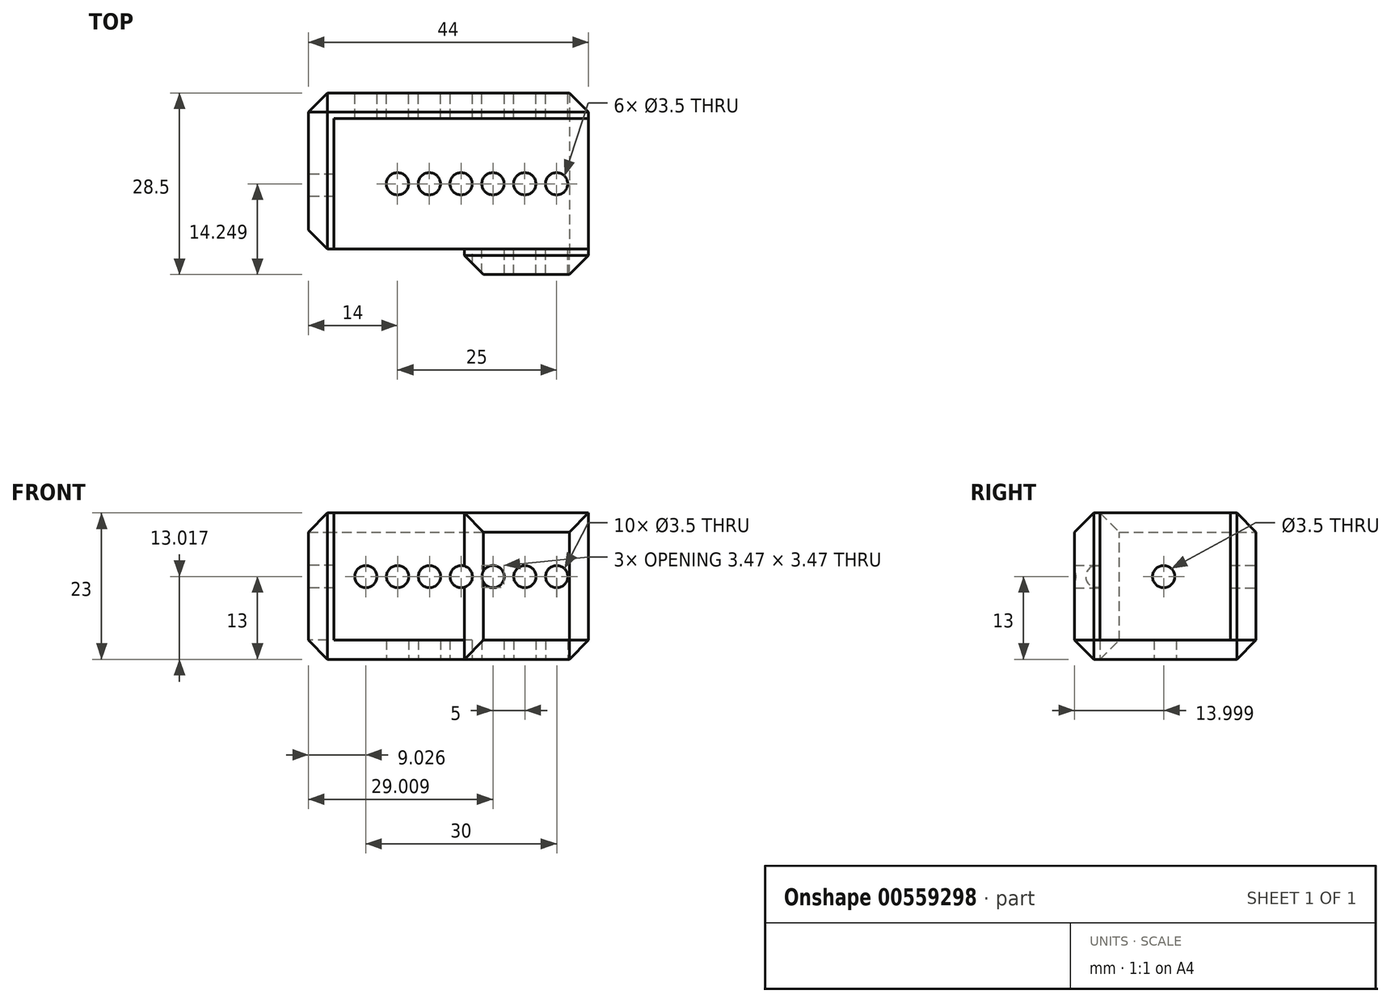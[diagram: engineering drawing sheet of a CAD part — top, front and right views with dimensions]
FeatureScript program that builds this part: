
annotation { "Feature Type Name" : "Feature", "Feature Type Description" : "" }
export const myFeature = defineFeature(function(context is Context, id is Id, definition is map)
    precondition{}
    {
        {
            var Q0;
            Q0=qCreatedBy(makeId("Top.planeOp"),FACE);
            var sketch = newSketch(context, id + "F0", { "sketchPlane" : qUnion([Q0])});
            skLineSegment(sketch, "E0", {"start": v(-54.8, 23.52) * mm, "end": v(-54.8, 3.02) * mm});
            skLineSegment(sketch, "E1", {"start": v(-54.8, 23.52) * mm, "end": v(-14.8, 23.52) * mm});
            skLineSegment(sketch, "E2", {"start": v(-54.8, 3.02) * mm, "end": v(-14.8, 3.02) * mm});
            skLineSegment(sketch, "E3", {"start": v(-14.8, 3.02) * mm, "end": v(-14.8, 23.52) * mm});
            skLineSegment(sketch, "E4", {"start": v(-58.8, 3.02) * mm, "end": v(-54.8, 3.02) * mm});
            skLineSegment(sketch, "E5", {"start": v(-14.8, 23.52) * mm, "end": v(-14.8, 27.52) * mm});
            skLineSegment(sketch, "E6", {"start": v(-14.8, 27.52) * mm, "end": v(-58.8, 27.52) * mm});
            skLineSegment(sketch, "E7", {"start": v(-58.8, 27.52) * mm, "end": v(-58.8, 3.02) * mm});
            skLineSegment(sketch, "E8", {"start": v(-54.8, 23.52) * mm, "end": v(-34.8, 3.02) * mm, "construction": true});
            skLineSegment(sketch, "E9", {"start": v(-34.8, 3.02) * mm, "end": v(-14.8, 23.52) * mm, "construction": true});
            skLineSegment(sketch, "E10", {"start": v(-14.8, 3.02) * mm, "end": v(-34.8, 23.52) * mm, "construction": true});
            skLineSegment(sketch, "E11", {"start": v(-34.8, 23.52) * mm, "end": v(-54.8, 3.02) * mm, "construction": true});
            skCircle(sketch, "E12", {"center": v(-24.8, 13.27) * mm, "radius": 1.75 * mm});
            skLineSegment(sketch, "E13", {"start": v(-24.8, 13.27) * mm, "end": v(-29.8, 13.27) * mm});
            skLineSegment(sketch, "E14", {"start": v(-29.8, 13.27) * mm, "end": v(-34.8, 13.27) * mm});
            skLineSegment(sketch, "E15", {"start": v(-34.8, 13.27) * mm, "end": v(-39.8, 13.27) * mm});
            skLineSegment(sketch, "E16", {"start": v(-39.8, 13.27) * mm, "end": v(-44.8, 13.27) * mm});
            skLineSegment(sketch, "E17", {"start": v(-24.8, 13.27) * mm, "end": v(-19.8, 13.27) * mm});
            skLineSegment(sketch, "E18", {"start": v(-19.8, 13.27) * mm, "end": v(-14.8, 13.27) * mm});
            skCircle(sketch, "E19", {"center": v(-39.8, 13.27) * mm, "radius": 1.75 * mm});
            skCircle(sketch, "E20", {"center": v(-34.8, 13.27) * mm, "radius": 1.75 * mm});
            skCircle(sketch, "E21", {"center": v(-19.8, 13.27) * mm, "radius": 1.75 * mm});
            skCircle(sketch, "E22", {"center": v(-29.8, 13.27) * mm, "radius": 1.75 * mm});
            skCircle(sketch, "E23", {"center": v(-44.8, 13.27) * mm, "radius": 1.75 * mm});
            skLineSegment(sketch, "E24", {"start": v(-14.8, 3.02) * mm, "end": v(-14.8, -0.98) * mm});
            skLineSegment(sketch, "E25", {"start": v(-14.8, -0.98) * mm, "end": v(-34.3, -0.98) * mm});
            skLineSegment(sketch, "E26", {"start": v(-34.3, -0.98) * mm, "end": v(-34.3, 3.02) * mm});
            skSolve(sketch);
        }
        {
            var Q0;
            Q0=makeQuery(id+"F0.imprint","IMPRINT",FACE,{"disambiguationData":[TD([[makeQuery(id+"F0.imprint","IMPRINT",EDGE,{"derivedFrom":sQuery(id+"F0.wireOp",EDGE,"E0")}),1.0]])]});
            extrude(context, id + "F1", {"entities" : qUnion([Q0]), "depth" : 3 * mm, "offsetDistance" : 25 * mm});
        }
        {
            var Q0;
            Q0=makeQuery(id+"F0.imprint","IMPRINT",FACE,{"disambiguationData":[TD([[makeQuery(id+"F0.imprint","IMPRINT",EDGE,{"derivedFrom":sQuery(id+"F0.wireOp",EDGE,"E0")}),-1.0]])]});
            var Q1;
            {var subQ0=sQuery(id+"F0.wireOp",EDGE,"E24");Q1=makeQuery(id+"F0.imprint","IMPRINT",FACE,{"disambiguationData":[TD([[makeQuery(id+"F0.imprint","IMPRINT",EDGE,{"derivedFrom":subQ0}),-1.0]])]});}
            extrude(context, id + "F2", {"entities" : qUnion([Q0, Q1]), "operationType" : NewBodyOperationType.ADD, "depth" : 23 * mm, "offsetDistance" : 25 * mm});
        }
        {
            var Q0;
            Q0=makeQuery(id+"F2.opExtrude","SWEPT_FACE",FACE,{"disambiguationData":[OSD([sQuery(id+"F0.wireOp",EDGE,"E6")])]});
            var sketch = newSketch(context, id + "F3", { "sketchPlane" : qUnion([Q0])});
            skLineSegment(sketch, "E27.bottom", {"start": v(14.8, 23) * mm, "end": v(58.8, 23) * mm});
            skLineSegment(sketch, "E27.top", {"start": v(14.8, 3) * mm, "end": v(58.8, 3) * mm});
            skLineSegment(sketch, "E27.left", {"start": v(14.8, 23) * mm, "end": v(14.8, 3) * mm});
            skLineSegment(sketch, "E27.right", {"start": v(58.8, 23) * mm, "end": v(58.8, 3) * mm});
            skLineSegment(sketch, "E28", {"start": v(49.78, 13) * mm, "end": v(44.78, 13) * mm, "construction": true});
            skLineSegment(sketch, "E29", {"start": v(44.78, 13) * mm, "end": v(39.78, 13) * mm, "construction": true});
            skLineSegment(sketch, "E30", {"start": v(39.78, 13) * mm, "end": v(34.78, 13) * mm, "construction": true});
            skLineSegment(sketch, "E31", {"start": v(34.78, 13) * mm, "end": v(29.78, 13) * mm, "construction": true});
            skLineSegment(sketch, "E32", {"start": v(29.78, 13) * mm, "end": v(24.78, 13) * mm, "construction": true});
            skLineSegment(sketch, "E33", {"start": v(24.78, 13) * mm, "end": v(19.78, 13) * mm, "construction": true});
            skLineSegment(sketch, "E34", {"start": v(19.78, 13) * mm, "end": v(14.78, 13) * mm, "construction": true});
            skCircle(sketch, "E35", {"center": v(19.78, 13) * mm, "radius": 1.75 * mm});
            skCircle(sketch, "E36", {"center": v(24.78, 13) * mm, "radius": 1.75 * mm});
            skCircle(sketch, "E37", {"center": v(29.78, 13) * mm, "radius": 1.75 * mm});
            skCircle(sketch, "E38", {"center": v(34.78, 13) * mm, "radius": 1.75 * mm});
            skCircle(sketch, "E39", {"center": v(39.78, 13) * mm, "radius": 1.75 * mm});
            skCircle(sketch, "E40", {"center": v(44.78, 13) * mm, "radius": 1.75 * mm});
            skCircle(sketch, "E41", {"center": v(49.78, 13) * mm, "radius": 1.75 * mm});
            skLineSegment(sketch, "E42", {"start": v(49.78, 13) * mm, "end": v(58.8, 13) * mm});
            skSolve(sketch);
        }
        {
            var Q0;
            Q0=makeQuery(id+"F3.imprint","IMPRINT",FACE,{"disambiguationData":[TD([[makeQuery(id+"F3.imprint","IMPRINT",EDGE,{"derivedFrom":sQuery(id+"F3.wireOp",EDGE,"E35")}),1.0]])]});
            var Q1;
            Q1=makeQuery(id+"F3.imprint","IMPRINT",FACE,{"disambiguationData":[TD([[makeQuery(id+"F3.imprint","IMPRINT",EDGE,{"derivedFrom":sQuery(id+"F3.wireOp",EDGE,"E36")}),1.0]])]});
            var Q2;
            Q2=makeQuery(id+"F3.imprint","IMPRINT",FACE,{"disambiguationData":[TD([[makeQuery(id+"F3.imprint","IMPRINT",EDGE,{"derivedFrom":sQuery(id+"F3.wireOp",EDGE,"E37")}),1.0]])]});
            var Q3;
            Q3=makeQuery(id+"F3.imprint","IMPRINT",FACE,{"disambiguationData":[TD([[makeQuery(id+"F3.imprint","IMPRINT",EDGE,{"derivedFrom":sQuery(id+"F3.wireOp",EDGE,"E38")}),1.0]])]});
            var Q4;
            Q4=makeQuery(id+"F3.imprint","IMPRINT",FACE,{"disambiguationData":[TD([[makeQuery(id+"F3.imprint","IMPRINT",EDGE,{"derivedFrom":sQuery(id+"F3.wireOp",EDGE,"E39")}),1.0]])]});
            var Q5;
            Q5=makeQuery(id+"F3.imprint","IMPRINT",FACE,{"disambiguationData":[TD([[makeQuery(id+"F3.imprint","IMPRINT",EDGE,{"derivedFrom":sQuery(id+"F3.wireOp",EDGE,"E40")}),1.0]])]});
            var Q6;
            Q6=makeQuery(id+"F3.imprint","IMPRINT",FACE,{"disambiguationData":[TD([[makeQuery(id+"F3.imprint","IMPRINT",EDGE,{"derivedFrom":sQuery(id+"F3.wireOp",EDGE,"E41")}),1.0]])]});
            extrude(context, id + "F4", {"entities" : qUnion([Q0, Q1, Q2, Q3, Q4, Q5, Q6]), "operationType" : NewBodyOperationType.REMOVE, "endBound" : BoundingType.THROUGH_ALL, "oppositeDirection" : true, "depth" : 25 * mm, "offsetDistance" : 25 * mm});
        }
        {
            var Q0;
            Q0=makeQuery(id+"F2.opExtrude","SWEPT_FACE",FACE,{"disambiguationData":[OSD([sQuery(id+"F0.wireOp",EDGE,"E7")])]});
            var sketch = newSketch(context, id + "F5", { "sketchPlane" : qUnion([Q0])});
            skLineSegment(sketch, "E43.bottom", {"start": v(-3.02, 23) * mm, "end": v(-23.02, 23) * mm});
            skLineSegment(sketch, "E43.top", {"start": v(-3.02, 3) * mm, "end": v(-23.02, 3) * mm});
            skLineSegment(sketch, "E43.left", {"start": v(-3.02, 23) * mm, "end": v(-3.02, 3) * mm});
            skLineSegment(sketch, "E43.right", {"start": v(-23.02, 23) * mm, "end": v(-23.02, 3) * mm});
            skLineSegment(sketch, "E44", {"start": v(-23.02, 3) * mm, "end": v(-3.02, 23) * mm});
            skLineSegment(sketch, "E45", {"start": v(-3.02, 3) * mm, "end": v(-23.02, 23) * mm});
            skCircle(sketch, "E46", {"center": v(-13.02, 13) * mm, "radius": 1.75 * mm});
            skSolve(sketch);
        }
        {
            var Q0;
            {var subQ0=sQuery(id+"F5.wireOp",EDGE,"E45");var subQ1=sQuery(id+"F5.wireOp",EDGE,"E44");var subQ2=makeQuery(id+"F5.imprint","INTERSECT",VERTEX,{"derivedFrom":[subQ1,subQ0]});Q0=makeQuery(id+"F5.imprint","IMPRINT",FACE,{"disambiguationData":[TD([[makeQuery(id+"F5.imprint","IMPRINT",EDGE,{"disambiguationData":[TD([[subQ2,-1.0]])],"derivedFrom":subQ1}),1.0]])]});}
            var Q1;
            {var subQ0=sQuery(id+"F5.wireOp",EDGE,"E46");var subQ1=sQuery(id+"F5.wireOp",EDGE,"E44");var subQ2=makeQuery(id+"F5.imprint","INTERSECT",VERTEX,{"disambiguationData":[OD(0.0)],"derivedFrom":[subQ1,subQ0]});Q1=makeQuery(id+"F5.imprint","IMPRINT",FACE,{"disambiguationData":[TD([[makeQuery(id+"F5.imprint","IMPRINT",EDGE,{"disambiguationData":[TD([[subQ2,-1.0]])],"derivedFrom":subQ1}),-1.0]])]});}
            var Q2;
            {var subQ0=sQuery(id+"F5.wireOp",EDGE,"E45");var subQ1=sQuery(id+"F5.wireOp",EDGE,"E44");var subQ2=makeQuery(id+"F5.imprint","INTERSECT",VERTEX,{"derivedFrom":[subQ1,subQ0]});Q2=makeQuery(id+"F5.imprint","IMPRINT",FACE,{"disambiguationData":[TD([[makeQuery(id+"F5.imprint","IMPRINT",EDGE,{"disambiguationData":[TD([[subQ2,-1.0]])],"derivedFrom":subQ1}),-1.0]])]});}
            var Q3;
            {var subQ0=sQuery(id+"F5.wireOp",EDGE,"E46");var subQ1=sQuery(id+"F5.wireOp",EDGE,"E44");var subQ2=makeQuery(id+"F5.imprint","INTERSECT",VERTEX,{"disambiguationData":[OD(0.0)],"derivedFrom":[subQ1,subQ0]});Q3=makeQuery(id+"F5.imprint","IMPRINT",FACE,{"disambiguationData":[TD([[makeQuery(id+"F5.imprint","IMPRINT",EDGE,{"disambiguationData":[TD([[subQ2,-1.0]])],"derivedFrom":subQ1}),1.0]])]});}
            extrude(context, id + "F6", {"entities" : qUnion([Q0, Q1, Q2, Q3]), "operationType" : NewBodyOperationType.REMOVE, "oppositeDirection" : true, "depth" : 25 * mm, "offsetDistance" : 25 * mm});
        }
        {
            var Q0;
            Q0=makeQuery(id+"F2.opExtrude","CAP_EDGE",EDGE,{"disambiguationData":[OSD([sQuery(id+"F0.wireOp",EDGE,"E6")])],"isStart":true});
            var Q1;
            Q1=makeQuery(id+"F2.opExtrude","SWEPT_EDGE",EDGE,{"disambiguationData":[OSD([sQuery(id+"F0.wireOp",EDGE,"E6"),sQuery(id+"F0.wireOp",EDGE,"E7")])]});
            var Q2;
            Q2=makeQuery(id+"F2.opExtrude","CAP_EDGE",EDGE,{"disambiguationData":[OSD([sQuery(id+"F0.wireOp",EDGE,"E7")])],"isStart":true});
            var Q3;
            Q3=makeQuery(id+"F2.boolean.opBoolean","MERGE",EDGE,{"derivedFrom":[makeQuery(id+"F1.opExtrude","CAP_EDGE",EDGE,{"disambiguationData":[OSD([sQuery(id+"F0.wireOp",EDGE,"E3")])],"isStart":true}),makeQuery(id+"F2.opExtrude","CAP_EDGE",EDGE,{"disambiguationData":[OSD([sQuery(id+"F0.wireOp",EDGE,"E5")])],"isStart":true}),makeQuery(id+"F2.opExtrude","CAP_EDGE",EDGE,{"disambiguationData":[OSD([sQuery(id+"F0.wireOp",EDGE,"E24")])],"isStart":true})]});
            var Q4;
            Q4=makeQuery(id+"F2.opExtrude","SWEPT_EDGE",EDGE,{"disambiguationData":[OSD([sQuery(id+"F0.wireOp",EDGE,"E5"),sQuery(id+"F0.wireOp",EDGE,"E6")])]});
            var Q5;
            Q5=makeQuery(id+"F2.opExtrude","CAP_EDGE",EDGE,{"disambiguationData":[OSD([sQuery(id+"F0.wireOp",EDGE,"E25")])],"isStart":true});
            var Q6;
            Q6=makeQuery(id+"F2.opExtrude","SWEPT_EDGE",EDGE,{"disambiguationData":[OSD([sQuery(id+"F0.wireOp",EDGE,"E24"),sQuery(id+"F0.wireOp",EDGE,"E25")])]});
            var Q7;
            Q7=makeQuery(id+"F2.opExtrude","SWEPT_EDGE",EDGE,{"disambiguationData":[OSD([sQuery(id+"F0.wireOp",EDGE,"E4"),sQuery(id+"F0.wireOp",EDGE,"E7")])]});
            var Q8;
            Q8=makeQuery(id+"F2.opExtrude","CAP_EDGE",EDGE,{"disambiguationData":[OSD([sQuery(id+"F0.wireOp",EDGE,"E7")])],"isStart":false});
            var Q9;
            Q9=makeQuery(id+"F2.opExtrude","CAP_EDGE",EDGE,{"disambiguationData":[OSD([sQuery(id+"F0.wireOp",EDGE,"E6")])],"isStart":false});
            var Q10;
            Q10=makeQuery(id+"F2.opExtrude","CAP_EDGE",EDGE,{"disambiguationData":[OSD([sQuery(id+"F0.wireOp",EDGE,"E25")])],"isStart":false});
            var Q11;
            {var subQ0=sQuery(id+"F0.wireOp",EDGE,"E26");var subQ1=sQuery(id+"F0.wireOp",EDGE,"E25");Q11=makeQuery(id+"F4.boolean.opBoolean","SPLIT",EDGE,{"disambiguationData":[TD([makeQuery(id+"F2.opExtrude","CAP_FACE",FACE,{"disambiguationData":[OSD([sQuery(id+"F0.wireOp",EDGE,"E2"),sQuery(id+"F0.wireOp",EDGE,"E24"),subQ1,subQ0])],"isStart":false})])],"derivedFrom":makeQuery(id+"F2.opExtrude","SWEPT_EDGE",EDGE,{"disambiguationData":[OSD([subQ1,subQ0])]})});}
            chamfer(context, id + "F7", {"entities" : qUnion([Q0, Q1, Q2, Q3, Q4, Q5, Q6, Q7, Q8, Q9, Q10, Q11]), "width" : 3 * mm, "tangentPropagation" : true});
        }
    });
